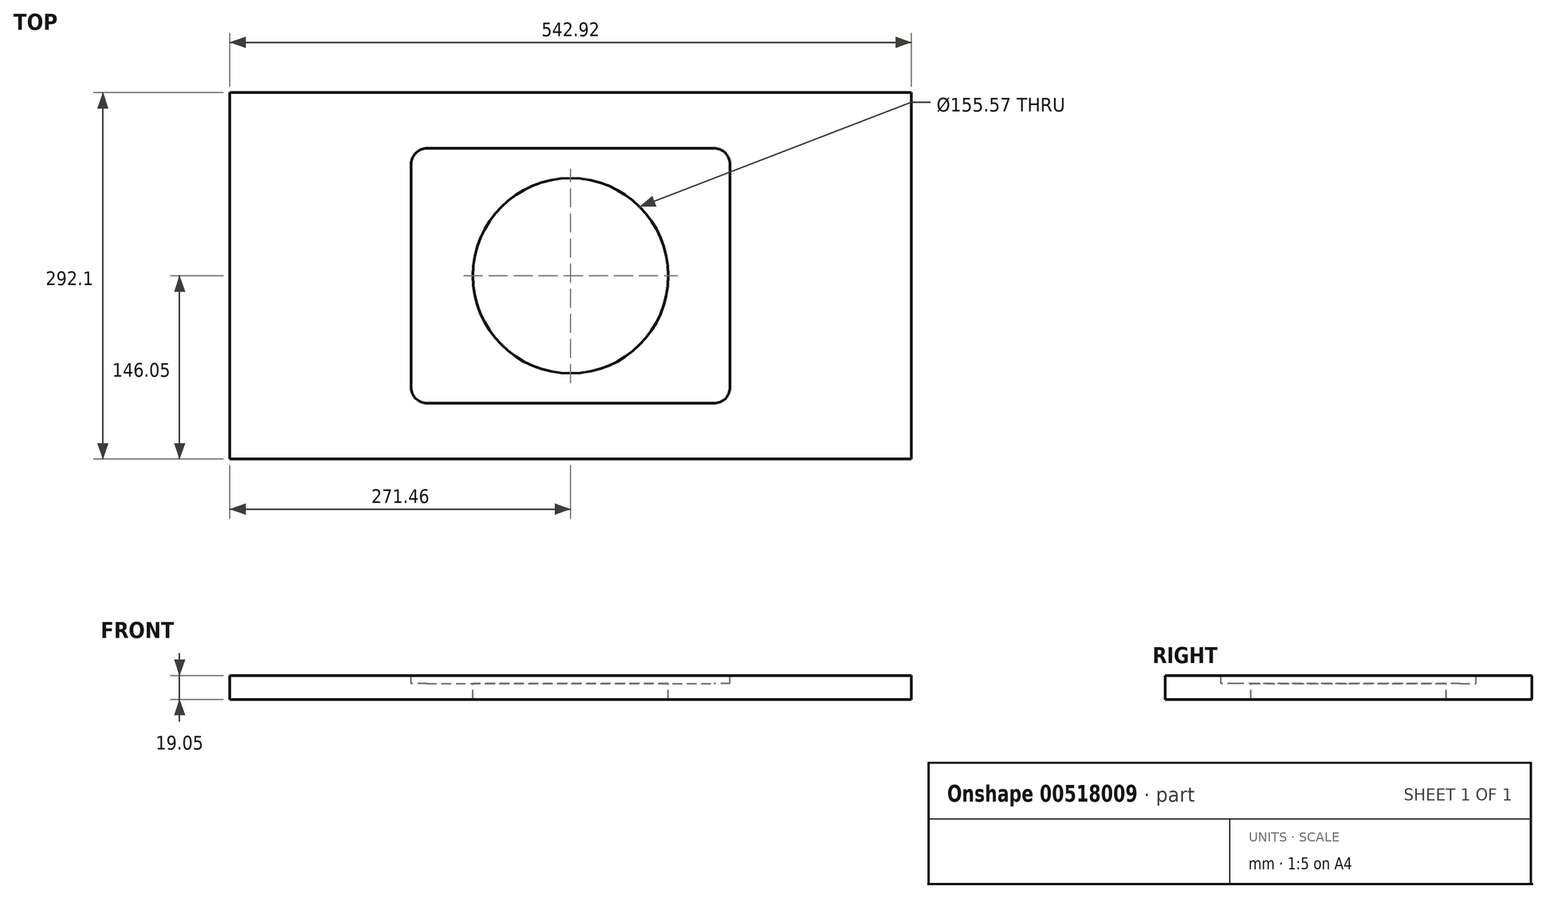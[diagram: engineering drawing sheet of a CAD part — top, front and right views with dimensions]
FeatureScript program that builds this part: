
annotation { "Feature Type Name" : "Feature", "Feature Type Description" : "" }
export const myFeature = defineFeature(function(context is Context, id is Id, definition is map)
    precondition{}
    {
        {
            var Q0;
            Q0=qCreatedBy(makeId("Top.planeOp"),FACE);
            var sketch = newSketch(context, id + "F0", { "sketchPlane" : qUnion([Q0])});
            skLineSegment(sketch, "E0.bottom", {"start": v(-271.46, 146.05) * mm, "end": v(271.46, 146.05) * mm});
            skLineSegment(sketch, "E0.top", {"start": v(-271.46, -146.05) * mm, "end": v(271.46, -146.05) * mm});
            skLineSegment(sketch, "E0.left", {"start": v(-271.46, 146.05) * mm, "end": v(-271.46, -146.05) * mm});
            skLineSegment(sketch, "E0.right", {"start": v(271.46, 146.05) * mm, "end": v(271.46, -146.05) * mm});
            skSolve(sketch);
        }
        {
            var Q0;
            Q0 = qSketchRegion(id + "F0", true);
            extrude(context, id + "F1", {"entities" : qUnion([Q0]), "depth" : 19.05 * mm, "offsetDistance" : 25.4 * mm});
        }
        {
            var Q0;
            Q0=makeQuery(id+"F1.opExtrude","CAP_FACE",FACE,{"disambiguationData":[OSD([sQuery(id+"F0.wireOp",EDGE,"E0.bottom"),sQuery(id+"F0.wireOp",EDGE,"E0.top"),sQuery(id+"F0.wireOp",EDGE,"E0.left"),sQuery(id+"F0.wireOp",EDGE,"E0.right")])],"isStart":false});
            var sketch = newSketch(context, id + "F2", { "sketchPlane" : qUnion([Q0])});
            skLineSegment(sketch, "E1.bottom", {"start": v(-127, 101.6) * mm, "end": v(127, 101.6) * mm});
            skLineSegment(sketch, "E1.top", {"start": v(-127, -101.6) * mm, "end": v(127, -101.6) * mm});
            skLineSegment(sketch, "E1.left", {"start": v(-127, 101.6) * mm, "end": v(-127, -101.6) * mm});
            skLineSegment(sketch, "E1.right", {"start": v(127, 101.6) * mm, "end": v(127, -101.6) * mm});
            skPoint(sketch, "E1.middle", {"position": v(0, 0) * mm});
            skSolve(sketch);
        }
        {
            var Q0;
            Q0 = qSketchRegion(id + "F2", true);
            extrude(context, id + "F3", {"entities" : qUnion([Q0]), "operationType" : NewBodyOperationType.REMOVE, "oppositeDirection" : true, "depth" : 6.35 * mm, "offsetDistance" : 25.4 * mm});
        }
        {
            var Q0;
            Q0=makeQuery(id+"F3.boolean.opBoolean","COPY",EDGE,{"derivedFrom":makeQuery(id+"F3.opExtrude","SWEPT_EDGE",EDGE,{"disambiguationData":[OSD([sQuery(id+"F2.wireOp",EDGE,"E1.top"),sQuery(id+"F2.wireOp",EDGE,"E1.right")])]})});
            var Q1;
            Q1=makeQuery(id+"F3.boolean.opBoolean","COPY",EDGE,{"derivedFrom":makeQuery(id+"F3.opExtrude","SWEPT_EDGE",EDGE,{"disambiguationData":[OSD([sQuery(id+"F2.wireOp",EDGE,"E1.top"),sQuery(id+"F2.wireOp",EDGE,"E1.left")])]})});
            var Q2;
            Q2=makeQuery(id+"F3.boolean.opBoolean","COPY",EDGE,{"derivedFrom":makeQuery(id+"F3.opExtrude","SWEPT_EDGE",EDGE,{"disambiguationData":[OSD([sQuery(id+"F2.wireOp",EDGE,"E1.bottom"),sQuery(id+"F2.wireOp",EDGE,"E1.left")])]})});
            var Q3;
            Q3=makeQuery(id+"F3.boolean.opBoolean","COPY",EDGE,{"derivedFrom":makeQuery(id+"F3.opExtrude","SWEPT_EDGE",EDGE,{"disambiguationData":[OSD([sQuery(id+"F2.wireOp",EDGE,"E1.bottom"),sQuery(id+"F2.wireOp",EDGE,"E1.right")])]})});
            fillet(context, id + "F4", {"entities" : qUnion([Q0, Q1, Q2, Q3]), "radius" : 12.7 * mm, "tangentPropagation" : true, "allowEdgeOverflow" : false});
        }
        {
            var Q0;
            Q0=makeQuery(id+"F3.boolean.opBoolean","COPY",FACE,{"derivedFrom":makeQuery(id+"F3.opExtrude","CAP_FACE",FACE,{"disambiguationData":[OSD([sQuery(id+"F2.wireOp",EDGE,"E1.bottom"),sQuery(id+"F2.wireOp",EDGE,"E1.top"),sQuery(id+"F2.wireOp",EDGE,"E1.left"),sQuery(id+"F2.wireOp",EDGE,"E1.right")])],"isStart":false})});
            var sketch = newSketch(context, id + "F5", { "sketchPlane" : qUnion([Q0])});
            skCircle(sketch, "E2", {"center": v(0, 0) * mm, "radius": 77.79 * mm});
            skSolve(sketch);
        }
        {
            var Q0;
            Q0 = qSketchRegion(id + "F5", true);
            extrude(context, id + "F6", {"entities" : qUnion([Q0]), "operationType" : NewBodyOperationType.REMOVE, "endBound" : BoundingType.UP_TO_NEXT, "oppositeDirection" : true, "depth" : 25.4 * mm, "offsetDistance" : 25.4 * mm});
        }
    });
